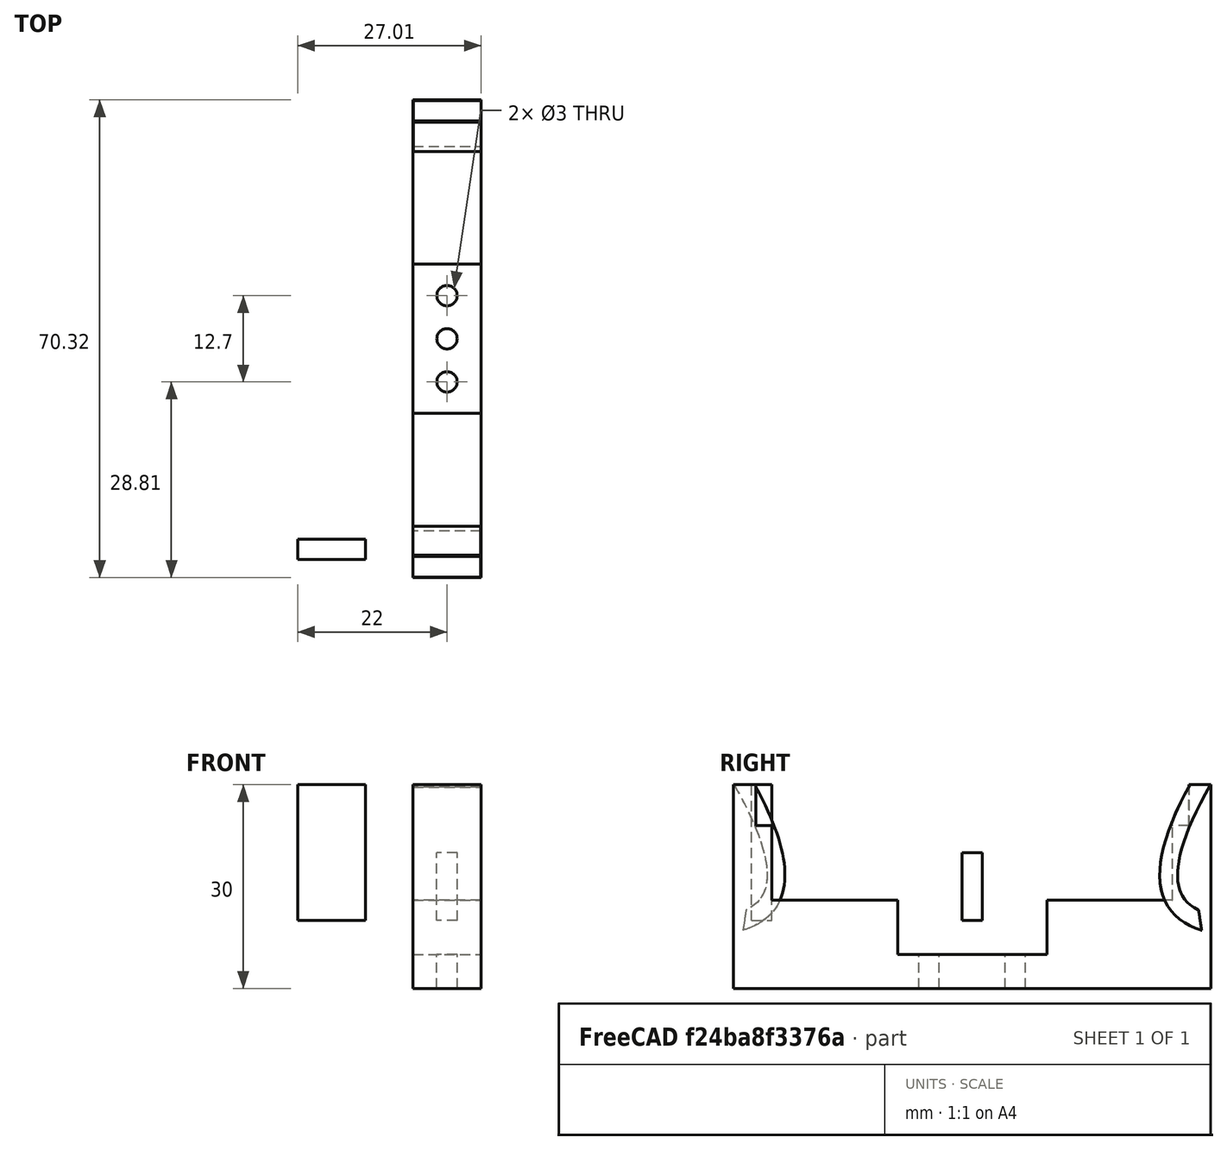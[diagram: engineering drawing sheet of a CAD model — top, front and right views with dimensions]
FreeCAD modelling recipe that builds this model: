
FCSTD DOCUMENT  (FreeCAD 0.18R16131 (Git))
Label: Gripper
License: All rights reserved
LicenseURL: http://en.wikipedia.org/wiki/All_rights_reserved
objects: Part::Box×14, Part::Cut×13, Part::Cylinder×7, Part::MultiFuse×4, Sketcher::SketchObject×4, Part::Sweep×2, Mesh::Feature×1
note: 44 computed .brp shape members not serialized (recipe doc carries the construction recipe); baked Part::Feature solids carry a one-line shape summary decoded from their .brp

FEATURE [Part::Box] Box  label="Base"
  AttacherType = Attacher::AttachEngine3D
  Height = 3
  Length = 20
  Width = 65
FEATURE [Part::Box] Box001  label="Arm1"
  AttacherType = Attacher::AttachEngine3D
  Height = 20
  Length = 20
  Placement = pos=(0,-2.66,0) rot=(-1,0,0;0rad)
  Width = 3.3
FEATURE [Part::Box] Box002  label="Arm2"
  AttacherType = Attacher::AttachEngine3D
  Height = 20
  Length = 20
  Placement = pos=(0,64.36,0) rot=(1,0,0;0rad)
  Width = 3.3
FEATURE [Part::Cylinder] Cylinder001  label="H1"
  Angle = 360
  AttacherType = Attacher::AttachEngine3D
  Height = 10
  Placement = pos=(3.65,32.5,-65) rot=(0,0,1;0rad)
  Radius = 1.5
FEATURE [Part::Cylinder] Cylinder003  label="H3"
  Angle = 360
  AttacherType = Attacher::AttachEngine3D
  Height = 10
  Placement = pos=(10,38.85,0) rot=(0,0,1;0rad)
  Radius = 1.5
FEATURE [Part::Cylinder] Cylinder004  label="H4"
  Angle = 360
  AttacherType = Attacher::AttachEngine3D
  Height = 10
  Placement = pos=(10,26.15,0) rot=(0,0,1;0rad)
  Radius = 1.5
FEATURE [Part::Cylinder] Cylinder  label="HRef"
  Angle = 360
  AttacherType = Attacher::AttachEngine3D
  Height = 10
  Placement = pos=(10,32.5,0) rot=(0,0,1;0rad)
  Radius = 1.5
FEATURE [Part::Cut] Cut
  Base = -> Box
  Tool = -> Cylinder001
FEATURE [Part::Cut] Cut001
  Base = -> Cut
  Tool = -> Cylinder004
FEATURE [Part::Box] Box003  label="Cube"
  AttacherType = Attacher::AttachEngine3D
  Height = 40
  Length = 5
  Placement = pos=(0,-10.5,-2) rot=(0,0,1;0rad)
  Width = 32
FEATURE [Part::Box] Box004  label="Cube001"
  AttacherType = Attacher::AttachEngine3D
  Height = 40
  Length = 5
  Placement = pos=(15,-10.5,-2) rot=(0,0,1;0rad)
  Width = 32
FEATURE [Part::Box] Box005  label="Cube002"
  AttacherType = Attacher::AttachEngine3D
  Height = 40
  Length = 5
  Placement = pos=(15,43.5,-2) rot=(0,0,1;0rad)
  Width = 32
FEATURE [Part::Box] Box006  label="Cube003"
  AttacherType = Attacher::AttachEngine3D
  Height = 40
  Length = 5
  Placement = pos=(0,43.5,-2) rot=(0,0,1;0rad)
  Width = 32
FEATURE [Part::Cut] Cut002
  Base = -> Cut001
  Tool = -> Cylinder003
FEATURE [Part::Cylinder] Cylinder002  label="H2"
  Angle = 360
  AttacherType = Attacher::AttachEngine3D
  Height = 10
  Placement = pos=(16.35,32.5,-32) rot=(0,0,1;0rad)
  Radius = 1.5
FEATURE [Part::Cut] Cut003
  Base = -> Cut002
  Tool = -> Cylinder002
FEATURE [Part::MultiFuse] Fusion
  Shapes = -> [Box001,Cut003,Box002]
FEATURE [Part::Cut] Cut004
  Base = -> Fusion
  Tool = -> Box003
FEATURE [Part::Cut] Cut005
  Base = -> Cut004
  Tool = -> Box004
FEATURE [Part::Cut] Cut006
  Base = -> Cut005
  Tool = -> Box005
FEATURE [Part::Cut] Cut007
  Base = -> Cut006
  Tool = -> Box006
FEATURE [Part::Box] Box007  label="Cube004"
  AttacherType = Attacher::AttachEngine3D
  Height = 10
  Length = 10
  Placement = pos=(-5,21.5,-2) rot=(0,0,1;0rad)
  Width = 22
FEATURE [Part::Cut] Cut008
  Base = -> Cut007
  Tool = -> Box007
FEATURE [Part::Box] Box008  label="Cube005"
  AttacherType = Attacher::AttachEngine3D
  Height = 10
  Length = 10
  Placement = pos=(15,21.5,-2) rot=(0,0,1;0rad)
  Width = 22
FEATURE [Part::Cut] Cut009
  Base = -> Cut008
  Tool = -> Box008
FEATURE [Part::Box] Box009  label="Cube006"
  AttacherType = Attacher::AttachEngine3D
  Height = 10.5
  Length = 10
  Placement = pos=(5,-2.66,-10) rot=(0,0,1;0rad)
  Width = 70.32
FEATURE [Part::Cylinder] Cylinder005  label="H005"
  Angle = 360
  AttacherType = Attacher::AttachEngine3D
  Height = 50
  Placement = pos=(10,38.85,-36) rot=(0,0,1;0rad)
  Radius = 1.5
FEATURE [Part::Cut] Cut010
  Base = -> Box009
  Tool = -> Cylinder005
FEATURE [Part::Cylinder] Cylinder006  label="H006"
  Angle = 360
  AttacherType = Attacher::AttachEngine3D
  Height = 50
  Placement = pos=(10,26.15,-30) rot=(0,0,1;0rad)
  Radius = 1.5
FEATURE [Part::Cut] Cut011
  Base = -> Cut010
  Tool = -> Cylinder006
FEATURE [Part::MultiFuse] Fusion001
  Shapes = -> [Cut011,Cut009]
FEATURE [Mesh::Feature] rcr_gripper
  Placement = pos=(0,60.5,0) rot=(1,0,0;0.05236rad)
FEATURE [Part::Box] Box010  label="Cube007"
  AttacherType = Attacher::AttachEngine3D
  Height = 8
  Length = 10
  Placement = pos=(5,21.5,-5) rot=(0,0,1;0rad)
  Width = 22
FEATURE [Part::Box] Box011  label="Cube008"
  AttacherType = Attacher::AttachEngine3D
  Height = 20
  Length = 10
  Placement = pos=(-12,0,0) rot=(0,0,1;0rad)
  Width = 3
FEATURE [Sketcher::SketchObject] Sketch
  sketch-geometry (6):
    g0: Circle [constr] CenterX=-0.000419539 CenterY=-0.000744833 CenterZ=0 NormalX=0 NormalY=0 NormalZ=1 AngleXU=0 Radius=2
    g1: Circle [constr] CenterX=16.5113 CenterY=9.28178 CenterZ=0 NormalX=0 NormalY=0 NormalZ=1 AngleXU=0 Radius=2
    g2: Circle [constr] CenterX=20.0078 CenterY=-0.0467425 CenterZ=0 NormalX=0 NormalY=0 NormalZ=1 AngleXU=0 Radius=2
    g3: BSplineCurve PolesCount=3 KnotsCount=2 Degree=2 IsPeriodic=0
    g4: GeomPoint [constr] X=-0.000419539 Y=-0.000744833 Z=0
    g5: GeomPoint [constr] X=20.0078 Y=-0.0467425 Z=0
  constraints (8):
    c: Radius(g0) = 2
    c: Equal(g0,g1)
    c: Equal(g0,g2)
    c: InternalAlignment(g0,g3)
    c: InternalAlignment(g1,g3)
    c: InternalAlignment(g2,g3)
    c: InternalAlignment(g4,g3)
    c: InternalAlignment(g5,g3)
FEATURE [Sketcher::SketchObject] Sketch001
  Placement = pos=(0,0,0) rot=(0.57735,0.57735,0.57735;2.0944rad)
  sketch-geometry (4):
    g0: LineSegment StartX=1.45285 StartY=4.97394 StartZ=0 EndX=-1.58527 EndY=4.97394 EndZ=0
    g1: LineSegment StartX=-1.58527 StartY=4.97394 StartZ=0 EndX=-1.58527 EndY=-5.00715 EndZ=0
    g2: LineSegment StartX=-1.58527 StartY=-5.00715 StartZ=0 EndX=1.45285 EndY=-5.00715 EndZ=0
    g3: LineSegment StartX=1.45285 StartY=-5.00715 StartZ=0 EndX=1.45285 EndY=4.97394 EndZ=0
  constraints (8):
    c: Coincident(g0,g1)
    c: Coincident(g1,g2)
    c: Coincident(g2,g3)
    c: Coincident(g3,g0)
    c: Horizontal(g0)
    c: Horizontal(g2)
    c: Vertical(g1)
    c: Vertical(g3)
FEATURE [Part::Sweep] Sweep
  Frenet = false
  Placement = pos=(10,-1,20) rot=(0,1,0;1.5708rad)
  Sections = -> [Sketch001]
  Solid = true
  Spine = -> Sketch [Edge1]
  Transition = 1
FEATURE [Sketcher::SketchObject] Sketch002
  sketch-geometry (6):
    g0: Circle [constr] CenterX=-0.000419539 CenterY=-0.000744833 CenterZ=0 NormalX=0 NormalY=0 NormalZ=1 AngleXU=0 Radius=2
    g1: Circle [constr] CenterX=16.5113 CenterY=9.28178 CenterZ=0 NormalX=0 NormalY=0 NormalZ=1 AngleXU=0 Radius=2
    g2: Circle [constr] CenterX=20.0078 CenterY=-0.0467425 CenterZ=0 NormalX=0 NormalY=0 NormalZ=1 AngleXU=0 Radius=2
    g3: BSplineCurve PolesCount=3 KnotsCount=2 Degree=2 IsPeriodic=0
    g4: GeomPoint [constr] X=-0.000419539 Y=-0.000744833 Z=0
    g5: GeomPoint [constr] X=20.0078 Y=-0.0467425 Z=0
  constraints (8):
    c: Radius(g0) = 2
    c: Equal(g0,g1)
    c: Equal(g0,g2)
    c: InternalAlignment(g0,g3)
    c: InternalAlignment(g1,g3)
    c: InternalAlignment(g2,g3)
    c: InternalAlignment(g4,g3)
    c: InternalAlignment(g5,g3)
FEATURE [Sketcher::SketchObject] Sketch003
  Placement = pos=(0,0,0) rot=(0.57735,0.57735,0.57735;2.0944rad)
  sketch-geometry (4):
    g0: LineSegment StartX=1.45285 StartY=4.97394 StartZ=0 EndX=-1.58527 EndY=4.97394 EndZ=0
    g1: LineSegment StartX=-1.58527 StartY=4.97394 StartZ=0 EndX=-1.58527 EndY=-5.00715 EndZ=0
    g2: LineSegment StartX=-1.58527 StartY=-5.00715 StartZ=0 EndX=1.45285 EndY=-5.00715 EndZ=0
    g3: LineSegment StartX=1.45285 StartY=-5.00715 StartZ=0 EndX=1.45285 EndY=4.97394 EndZ=0
  constraints (8):
    c: Coincident(g0,g1)
    c: Coincident(g1,g2)
    c: Coincident(g2,g3)
    c: Coincident(g3,g0)
    c: Horizontal(g0)
    c: Horizontal(g2)
    c: Vertical(g1)
    c: Vertical(g3)
FEATURE [Part::Sweep] Sweep001
  Frenet = false
  Placement = pos=(10,66,20) rot=(0.707107,0,-0.707107;3.14159rad)
  Sections = -> [Sketch003]
  Solid = true
  Spine = -> Sketch002 [Edge1]
  Transition = 1
FEATURE [Part::Cut] Cut012
  Base = -> Fusion001
  Tool = -> Box010
FEATURE [Part::MultiFuse] Fusion002
  Shapes = -> [Cut012,Sweep,Sweep001]
FEATURE [Part::Box] Box012  label="Fill1"
  AttacherType = Attacher::AttachEngine3D
  Height = 14
  Length = 10
  Placement = pos=(5,-1,0) rot=(0,0,1;0rad)
  Width = 4
FEATURE [Part::Box] Box013  label="Fill2"
  AttacherType = Attacher::AttachEngine3D
  Height = 14
  Length = 10
  Placement = pos=(5,62,0) rot=(0,0,1;0rad)
  Width = 4
FEATURE [Part::MultiFuse] Fusion003
  Shapes = -> [Box012,Box013,Fusion002]
